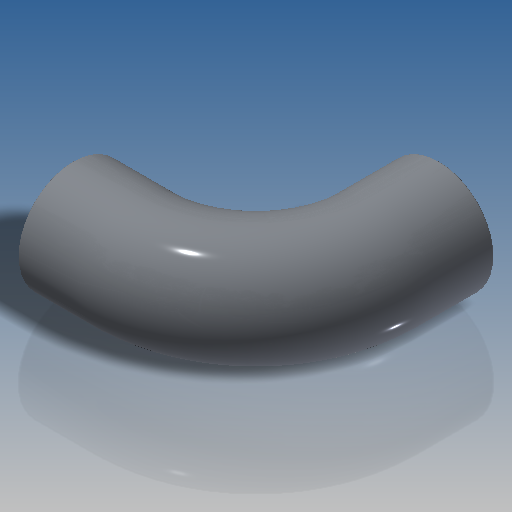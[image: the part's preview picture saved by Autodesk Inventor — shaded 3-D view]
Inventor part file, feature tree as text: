
AUTODESK INVENTOR PART (.ipt)
format: ipt  version: 2019.4 (Build 234330000, 330)  size: 298,496 bytes
history: native  units: in
note: dims shown in document units (in); Inventor stores cm internally (conversion verified against a paired STEP export)
features: sketch x2, extrude x2, plane x1, sweep x1, pattern_circular x1, fillet x1
ambient origin geometry x8: Origin, YZ Plane, XZ Plane, XY Plane, X Axis, Y Axis, Z Axis, Center Point
bodies: Solid1 (feature_tree)
feature tree (8):
  sketch  "Sketch2"  dims[d0=0.1575in d1=0.315in]
  plane  "Work Plane1"
  sketch  "Sketch3"  dims[d2=0.2835in d3=0.189in d4=45.0deg d5=0.063in d6=0.0252in d7=0.1113in d8=0.0787in d9=0.0539in d10=0.0in d11=0.0in d12=0.315in d13=0.0in d14=0.063in d15=0.0in d16=0.7874in d17=90.0deg d19=0.0039in d20=0.0in d21=0.0in]
  sweep  "Sweep1"
  extrude  "Extrusion1"  Depth=0.189in
  extrude  "Extrusion2"  TaperAngle=45.0deg  [1 undecoded]
  pattern_circular  "Circular Pattern1"  [2 undecoded]
  fillet  "Fillet1"  Radius=0.0252in
note: 3 required parameter values undecoded (feature->parameter linkage not recoverable at this tier; creation-order binding heuristic only, values carry confidence <= 0.55)
